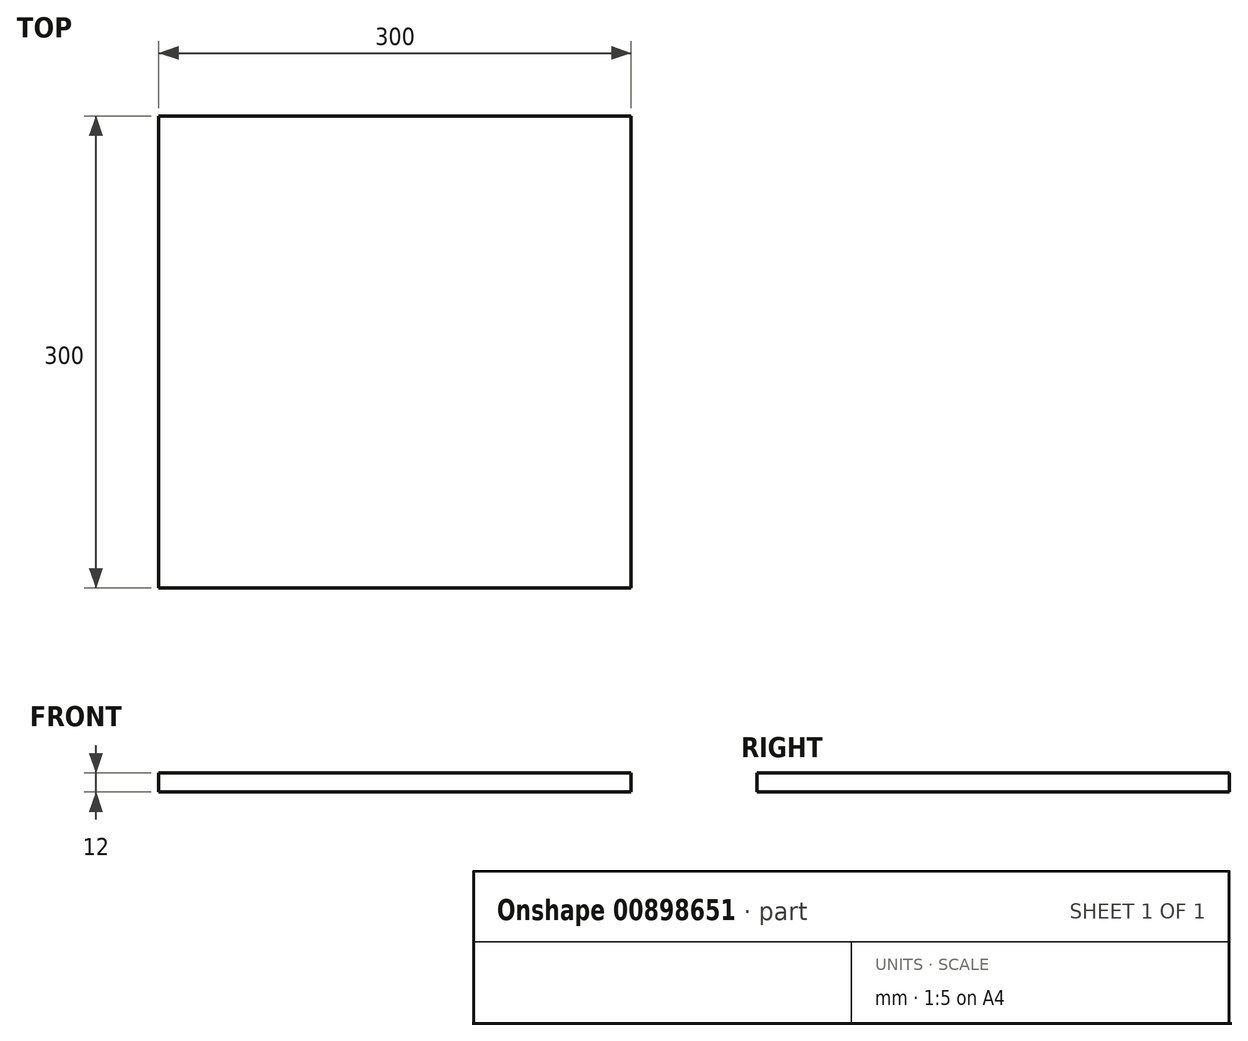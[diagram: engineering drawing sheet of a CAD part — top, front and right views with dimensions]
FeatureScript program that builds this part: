
annotation { "Feature Type Name" : "Feature", "Feature Type Description" : "" }
export const myFeature = defineFeature(function(context is Context, id is Id, definition is map)
    precondition{}
    {
        {
            var Q0;
            Q0=qCreatedBy(makeId("Top.planeOp"),FACE);
            var sketch = newSketch(context, id + "F0", { "sketchPlane" : qUnion([Q0])});
            skLineSegment(sketch, "E0.bottom", {"start": v(150, 150) * mm, "end": v(-150, 150) * mm});
            skLineSegment(sketch, "E0.top", {"start": v(150, -150) * mm, "end": v(-150, -150) * mm});
            skLineSegment(sketch, "E0.left", {"start": v(150, 150) * mm, "end": v(150, -150) * mm});
            skLineSegment(sketch, "E0.right", {"start": v(-150, 150) * mm, "end": v(-150, -150) * mm});
            skPoint(sketch, "E0.middle", {"position": v(0, 0) * mm});
            skSolve(sketch);
        }
        {
            var Q0;
            Q0=makeQuery(id+"F0.imprint","IMPRINT",FACE,{"disambiguationData":[TD([[makeQuery(id+"F0.imprint","IMPRINT",EDGE,{"derivedFrom":sQuery(id+"F0.wireOp",EDGE,"E0.bottom")}),1.0]])]});
            extrude(context, id + "F1", {"entities" : qUnion([Q0]), "depth" : 12 * mm, "offsetDistance" : 25 * mm});
        }
    });
